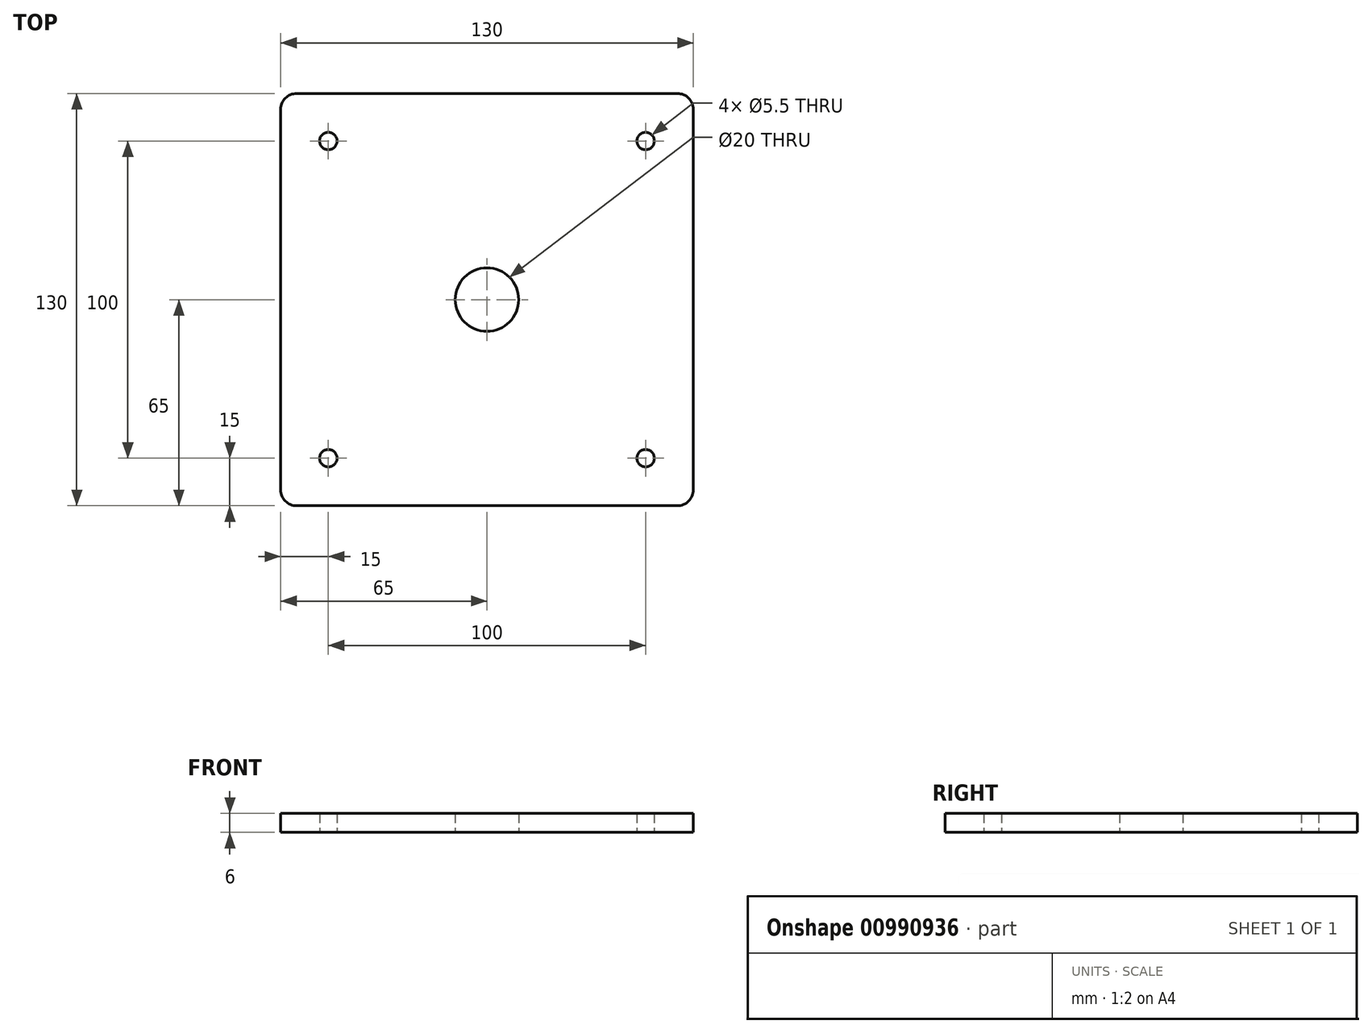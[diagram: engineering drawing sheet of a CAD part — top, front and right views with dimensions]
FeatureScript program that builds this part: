
annotation { "Feature Type Name" : "Feature", "Feature Type Description" : "" }
export const myFeature = defineFeature(function(context is Context, id is Id, definition is map)
    precondition{}
    {
        {
            var Q0;
            Q0=qCreatedBy(makeId("Top.planeOp"),FACE);
            var sketch = newSketch(context, id + "F0", { "sketchPlane" : qUnion([Q0])});
            skLineSegment(sketch, "E0.bottom", {"start": v(60, -65) * mm, "end": v(-60, -65) * mm});
            skLineSegment(sketch, "E0.top", {"start": v(60, 65) * mm, "end": v(-60, 65) * mm});
            skLineSegment(sketch, "E0.left", {"start": v(65, -60) * mm, "end": v(65, 60) * mm});
            skLineSegment(sketch, "E0.right", {"start": v(-65, -60) * mm, "end": v(-65, 60) * mm});
            skPoint(sketch, "E0.middle", {"position": v(0, 0) * mm});
            skCircle(sketch, "E1", {"center": v(-50, 50) * mm, "radius": 2.75 * mm});
            skCircle(sketch, "E2.MirrorC", {"center": v(50, 50) * mm, "radius": 2.75 * mm});
            skCircle(sketch, "E3.MirrorC", {"center": v(-50, -50) * mm, "radius": 2.75 * mm});
            skCircle(sketch, "E4.MirrorC", {"center": v(50, -50) * mm, "radius": 2.75 * mm});
            skPoint(sketch, "E5.visualSharp", {"position": v(-65, 65) * mm});
            skArc(sketch, "E5.filletArc", {"start": v(-60, 65) * mm, "mid": v(-63.54, 63.54) * mm, "end": v(-65, 60) * mm});
            skPoint(sketch, "E6.visualSharp", {"position": v(65, 65) * mm});
            skArc(sketch, "E6.filletArc", {"start": v(65, 60) * mm, "mid": v(63.54, 63.54) * mm, "end": v(60, 65) * mm});
            skPoint(sketch, "E7.visualSharp", {"position": v(65, -65) * mm});
            skArc(sketch, "E7.filletArc", {"start": v(60, -65) * mm, "mid": v(63.54, -63.54) * mm, "end": v(65, -60) * mm});
            skPoint(sketch, "E8.visualSharp", {"position": v(-65, -65) * mm});
            skArc(sketch, "E8.filletArc", {"start": v(-65, -60) * mm, "mid": v(-63.54, -63.54) * mm, "end": v(-60, -65) * mm});
            skCircle(sketch, "E9", {"center": v(0, 0) * mm, "radius": 10 * mm});
            skSolve(sketch);
        }
        {
            var Q0;
            Q0 = qSketchRegion(id + "F0", true);
            extrude(context, id + "F1", {"entities" : qUnion([Q0]), "depth" : 6 * mm, "offsetDistance" : 25 * mm});
        }
    });
